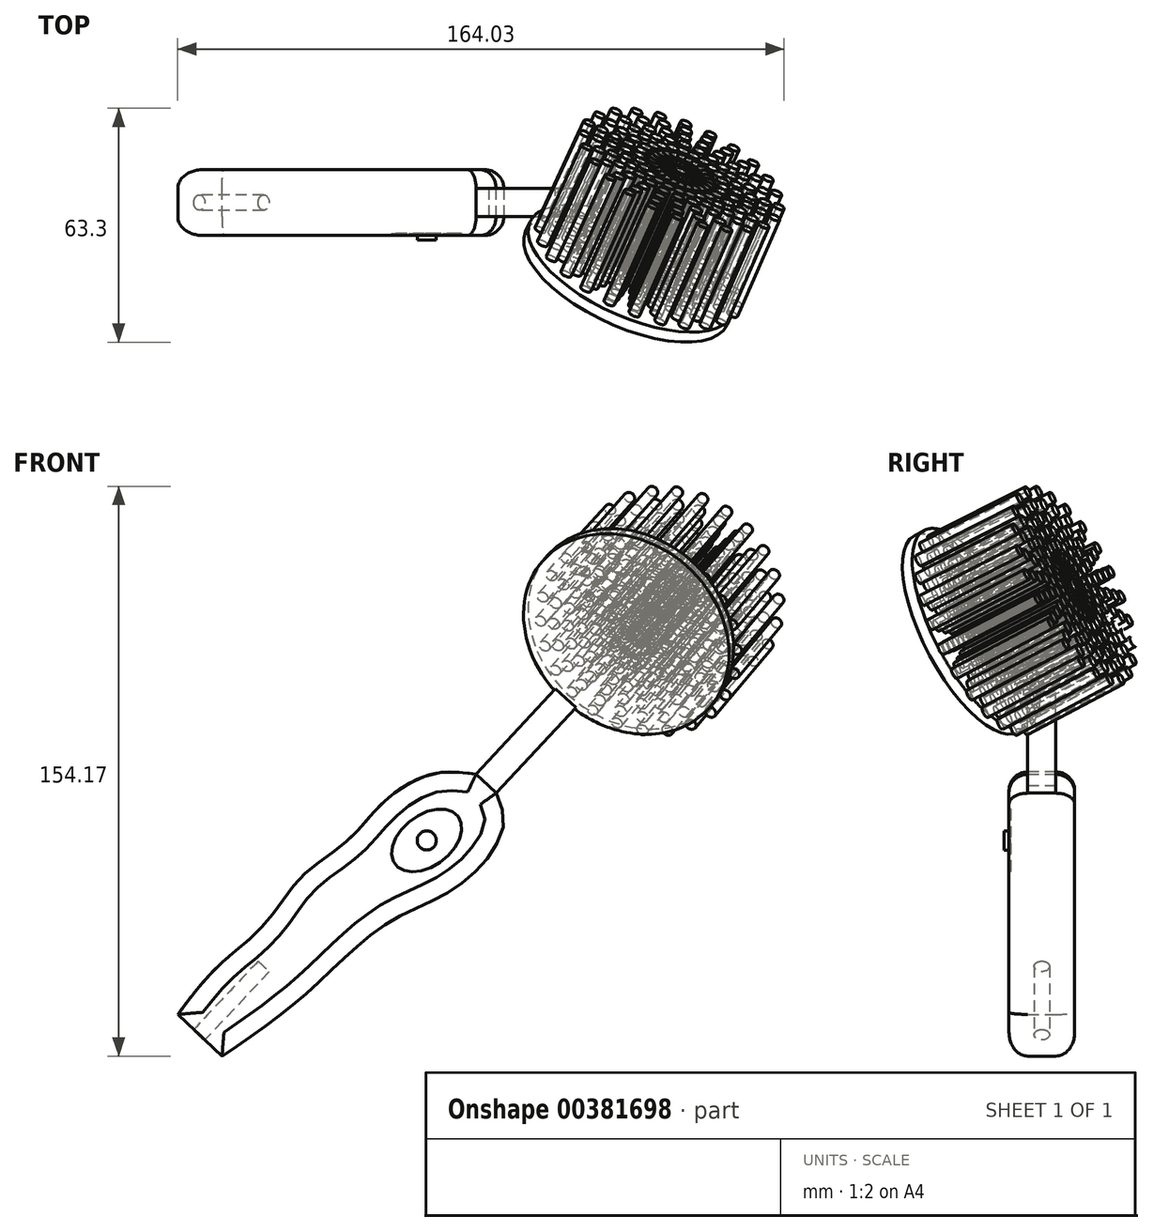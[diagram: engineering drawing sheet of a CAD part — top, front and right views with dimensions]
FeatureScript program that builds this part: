
annotation { "Feature Type Name" : "Feature", "Feature Type Description" : "" }
export const myFeature = defineFeature(function(context is Context, id is Id, definition is map)
    precondition{}
    {
        {
            var Q0;
            Q0=qCreatedBy(makeId("Front.planeOp"),FACE);
            var sketch = newSketch(context, id + "F0", { "sketchPlane" : qUnion([Q0])});
            skLineSegment(sketch, "E0", {"start": v(-5.4, 17.89) * mm, "end": v(0, 12.8) * mm});
            skLineSegment(sketch, "E1", {"start": v(-86.13, -47.06) * mm, "end": v(-74.15, -58.34) * mm});
            skFitSpline(sketch, "E2", {"points": [v(-86.13, -47.06) * mm, v(-75.3, -34.12) * mm, v(-62.36, -22.36) * mm, v(-53.18, -10.35) * mm, v(-40.24, 0) * mm, v(-29.65, 11.06) * mm, v(-16.7, 18.12) * mm, v(-5.4, 17.89) * mm], "startDerivative": vector(66.75, 89.58) * mm, "endDerivative": vector(90.32, -12.97) * mm});
            skFitSpline(sketch, "E3", {"points": [v(0, 12.8) * mm, v(1.88, 3.53) * mm, v(-10.12, -12.24) * mm, v(-29.42, -22.36) * mm, v(-51.3, -41.42) * mm, v(-74.15, -58.34) * mm], "startDerivative": vector(28.86, -64.08) * mm, "endDerivative": vector(-99.9, -67.33) * mm});
            skSolve(sketch);
        }
        {
            var Q0;
            Q0=makeQuery(id+"F0.imprint","IMPRINT",FACE,{"disambiguationData":[TD([[makeQuery(id+"F0.imprint","IMPRINT",EDGE,{"derivedFrom":sQuery(id+"F0.wireOp",EDGE,"E0")}),-1.0]])]});
            extrude(context, id + "F1", {"entities" : qUnion([Q0]), "depth" : 8.9 * mm});
        }
        {
            var Q0;
            Q0=makeQuery(id+"F1.opExtrude","CAP_FACE",FACE,{"disambiguationData":[OSD([sQuery(id+"F0.wireOp",EDGE,"E0"),sQuery(id+"F0.wireOp",EDGE,"E1"),sQuery(id+"F0.wireOp",EDGE,"E2"),sQuery(id+"F0.wireOp",EDGE,"E3")])],"isStart":true});
            extrude(context, id + "F2", {"entities" : qUnion([Q0]), "operationType" : NewBodyOperationType.ADD, "depth" : 8.9 * mm});
        }
        {
            var Q0;
            Q0=makeQuery(id+"F1.opExtrude","CAP_FACE",FACE,{"disambiguationData":[OSD([sQuery(id+"F0.wireOp",EDGE,"E0"),sQuery(id+"F0.wireOp",EDGE,"E1"),sQuery(id+"F0.wireOp",EDGE,"E2"),sQuery(id+"F0.wireOp",EDGE,"E3")])],"isStart":false});
            var Q1;
            Q1=makeQuery(id+"F2.opExtrude","CAP_FACE",FACE,{"disambiguationData":[OSD([sQuery(id+"F0.wireOp",EDGE,"E0"),sQuery(id+"F0.wireOp",EDGE,"E1"),sQuery(id+"F0.wireOp",EDGE,"E2"),sQuery(id+"F0.wireOp",EDGE,"E3")])],"isStart":false});
            fillet(context, id + "F3", {"entities" : qUnion([Q0, Q1]), "radius" : 5.08 * mm, "tangentPropagation" : true, "allowEdgeOverflow" : false});
        }
        {
            var Q0;
            Q0=qCreatedBy(makeId("Front.planeOp"),FACE);
            var sketch = newSketch(context, id + "F4", { "sketchPlane" : qUnion([Q0])});
            skLineSegment(sketch, "E4", {"start": v(-5.42, 17.88) * mm, "end": v(16, 41) * mm});
            skLineSegment(sketch, "E5", {"start": v(0, 12.81) * mm, "end": v(21.66, 36.03) * mm});
            skLineSegment(sketch, "E6", {"start": v(21.66, 36.03) * mm, "end": v(16, 41) * mm});
            skLineSegment(sketch, "E7", {"start": v(-5.42, 17.88) * mm, "end": v(0, 12.81) * mm});
            skSolve(sketch);
        }
        {
            var Q0;
            Q0=makeQuery(id+"F4.imprint","IMPRINT",FACE,{"disambiguationData":[TD([[makeQuery(id+"F4.imprint","IMPRINT",EDGE,{"derivedFrom":sQuery(id+"F4.wireOp",EDGE,"E4")}),-1.0]])]});
            extrude(context, id + "F5", {"entities" : qUnion([Q0]), "operationType" : NewBodyOperationType.ADD, "depth" : 3.8 * mm});
        }
        {
            var Q0;
            Q0=makeQuery(id+"F5.opExtrude","CAP_FACE",FACE,{"disambiguationData":[OSD([sQuery(id+"F4.wireOp",EDGE,"E4"),sQuery(id+"F4.wireOp",EDGE,"E5"),sQuery(id+"F4.wireOp",EDGE,"E6"),sQuery(id+"F4.wireOp",EDGE,"E7")])],"isStart":true});
            extrude(context, id + "F6", {"entities" : qUnion([Q0]), "operationType" : NewBodyOperationType.ADD, "depth" : 3.8 * mm});
        }
        {
            var Q0;
            {var subQ0=sQuery(id+"F4.wireOp",EDGE,"E6");Q0=makeQuery(id+"F6.boolean.opBoolean","MERGE",FACE,{"derivedFrom":[makeQuery(id+"F5.opExtrude","SWEPT_FACE",FACE,{"disambiguationData":[OSD([subQ0])]}),makeQuery(id+"F6.opExtrude","SWEPT_FACE",FACE,{"disambiguationData":[OSD([subQ0])]})]});}
            var sketch = newSketch(context, id + "F7", { "sketchPlane" : qUnion([Q0])});
            skLineSegment(sketch, "E8", {"start": v(-11.33, 3.81) * mm, "end": v(-11.33, -3.81) * mm, "construction": true});
            skSolve(sketch);
        }
        {
            var Q0;
            Q0=makeQuery(id+"F5.opExtrude","CAP_EDGE",EDGE,{"disambiguationData":[OSD([sQuery(id+"F4.wireOp",EDGE,"E6")])],"isStart":false});
            cPlane(context, id + "F8", {"entities" : qUnion([Q0]), "cplaneType" : CPlaneType.LINE_ANGLE, "offset" : 25.4 * mm, "angle" : 35 * degree, "oppositeDirection" : true, "width" : 152.4 * mm, "height" : 152.4 * mm});
        }
        {
            var Q0;
            Q0=qCreatedBy(id+"F8.planeOp",FACE);
            var sketch = newSketch(context, id + "F9", { "sketchPlane" : qUnion([Q0])});
            skCircle(sketch, "E9", {"center": v(29.65, 59.02) * mm, "radius": 30.06 * mm});
            skSolve(sketch);
        }
        {
            var Q0;
            Q0=makeQuery(id+"F9.imprint","IMPRINT",FACE,{"disambiguationData":[TD([[makeQuery(id+"F9.imprint","IMPRINT",EDGE,{"derivedFrom":sQuery(id+"F9.wireOp",EDGE,"E9")}),1.0]])]});
            extrude(context, id + "F10", {"entities" : qUnion([Q0]), "operationType" : NewBodyOperationType.ADD, "oppositeDirection" : true, "depth" : 3.3 * mm});
        }
        {
            var Q0;
            Q0=makeQuery(id+"F10.opExtrude","CAP_FACE",FACE,{"disambiguationData":[OSD([sQuery(id+"F9.wireOp",EDGE,"E9")])],"isStart":false});
            var sketch = newSketch(context, id + "F11", { "sketchPlane" : qUnion([Q0])});
            skLineSegment(sketch, "E10", {"start": v(-50.72, 80.45) * mm, "end": v(-10.25, 36.04) * mm, "construction": true});
            skLineSegment(sketch, "E11", {"start": v(-30.49, 58.25) * mm, "end": v(-7.43, 79.26) * mm, "construction": true});
            skLineSegment(sketch, "E12", {"start": v(-30.49, 58.25) * mm, "end": v(-51.87, 38.77) * mm, "construction": true});
            skSolve(sketch);
        }
        {
            var Q0;
            Q0=makeQuery(id+"F11.imprint","IMPRINT",FACE,{"disambiguationData":[TD([[makeQuery(id+"F11.imprint","IMPRINT",EDGE,{"derivedFrom":makeQuery(id+"F10.opExtrude","CAP_EDGE",EDGE,{"disambiguationData":[OSD([sQuery(id+"F9.wireOp",EDGE,"E9")])],"isStart":false})}),-1.0]])]});
            cPlane(context, id + "F12", {"entities" : qUnion([Q0]), "cplaneType" : CPlaneType.OFFSET, "offset" : 31.75 * mm, "width" : 152.4 * mm, "height" : 152.4 * mm});
        }
        {
            var Q0;
            Q0=qCreatedBy(id+"F12.planeOp",FACE);
            var sketch = newSketch(context, id + "F13", { "sketchPlane" : qUnion([Q0])});
            skCircle(sketch, "E13", {"center": v(-31.35, 57.04) * mm, "radius": 1.65 * mm});
            skCircle(sketch, "E14", {"center": v(-28.64, 54) * mm, "radius": 1.65 * mm});
            skCircle(sketch, "E15", {"center": v(-26, 50.91) * mm, "radius": 1.65 * mm});
            skCircle(sketch, "E16", {"center": v(-23.19, 47.99) * mm, "radius": 1.65 * mm});
            skCircle(sketch, "E17", {"center": v(-20.63, 44.83) * mm, "radius": 1.65 * mm});
            skCircle(sketch, "E18", {"center": v(-17.78, 41.94) * mm, "radius": 1.65 * mm});
            skCircle(sketch, "E19", {"center": v(-15.07, 38.9) * mm, "radius": 1.65 * mm});
            skCircle(sketch, "E20", {"center": v(-12.28, 36.13) * mm, "radius": 1.52 * mm});
            skSolve(sketch);
        }
        {
            var Q0;
            Q0=makeQuery(id+"F13.imprint","IMPRINT",FACE,{"disambiguationData":[TD([[makeQuery(id+"F13.imprint","IMPRINT",EDGE,{"derivedFrom":sQuery(id+"F13.wireOp",EDGE,"E13")}),1.0]])]});
            var Q1;
            Q1=makeQuery(id+"F13.imprint","IMPRINT",FACE,{"disambiguationData":[TD([[makeQuery(id+"F13.imprint","IMPRINT",EDGE,{"derivedFrom":sQuery(id+"F13.wireOp",EDGE,"E14")}),1.0]])]});
            var Q2;
            Q2=makeQuery(id+"F13.imprint","IMPRINT",FACE,{"disambiguationData":[TD([[makeQuery(id+"F13.imprint","IMPRINT",EDGE,{"derivedFrom":sQuery(id+"F13.wireOp",EDGE,"E15")}),1.0]])]});
            var Q3;
            Q3=makeQuery(id+"F13.imprint","IMPRINT",FACE,{"disambiguationData":[TD([[makeQuery(id+"F13.imprint","IMPRINT",EDGE,{"derivedFrom":sQuery(id+"F13.wireOp",EDGE,"E16")}),1.0]])]});
            var Q4;
            Q4=makeQuery(id+"F13.imprint","IMPRINT",FACE,{"disambiguationData":[TD([[makeQuery(id+"F13.imprint","IMPRINT",EDGE,{"derivedFrom":sQuery(id+"F13.wireOp",EDGE,"E17")}),1.0]])]});
            var Q5;
            Q5=makeQuery(id+"F13.imprint","IMPRINT",FACE,{"disambiguationData":[TD([[makeQuery(id+"F13.imprint","IMPRINT",EDGE,{"derivedFrom":sQuery(id+"F13.wireOp",EDGE,"E18")}),1.0]])]});
            var Q6;
            Q6=makeQuery(id+"F13.imprint","IMPRINT",FACE,{"disambiguationData":[TD([[makeQuery(id+"F13.imprint","IMPRINT",EDGE,{"derivedFrom":sQuery(id+"F13.wireOp",EDGE,"E19")}),1.0]])]});
            var Q7;
            Q7=makeQuery(id+"F13.imprint","IMPRINT",FACE,{"disambiguationData":[TD([[makeQuery(id+"F13.imprint","IMPRINT",EDGE,{"derivedFrom":sQuery(id+"F13.wireOp",EDGE,"E20")}),1.0]])]});
            extrude(context, id + "F14", {"entities" : qUnion([Q0, Q1, Q2, Q3, Q4, Q5, Q6, Q7]), "operationType" : NewBodyOperationType.ADD, "oppositeDirection" : true, "depth" : 31.62 * mm});
        }
        {
            var Q0;
            Q0=qCreatedBy(id+"F12.planeOp",FACE);
            var sketch = newSketch(context, id + "F15", { "sketchPlane" : qUnion([Q0])});
            skPoint(sketch, "E21", {"position": v(-31.35, 57.04) * mm});
            skSolve(sketch);
        }
        {
            var Q0;
            Q0=sQuery(id+"F11.wireOp",EDGE,"E12");
            var Q1;
            Q1=sQuery(id+"F15.wireOp",VERTEX,"E21");
            cPlane(context, id + "F16", {"entities" : qUnion([Q0, Q1]), "cplaneType" : CPlaneType.LINE_ANGLE, "offset" : 25.4 * mm, "angle" : 0 * degree, "width" : 152.4 * mm, "height" : 152.4 * mm});
        }
        {
            var Q0;
            Q0=qCreatedBy(id+"F16.planeOp",FACE);
            var sketch = newSketch(context, id + "F17", { "sketchPlane" : qUnion([Q0])});
            skLineSegment(sketch, "E22", {"start": v(-45.25, 93.19) * mm, "end": v(-30.63, 58.2) * mm, "construction": true});
            skLineSegment(sketch, "E23", {"start": v(53.65, 19.52) * mm, "end": v(22.06, 16.93) * mm, "construction": true});
            skSolve(sketch);
        }
        {
            var Q0;
            Q0=makeQuery(id+"F14.opExtrude","SWEPT_BODY",BODY,{"disambiguationData":[OSD([sQuery(id+"F13.wireOp",EDGE,"E13")])]});
            var Q1;
            Q1=makeQuery(id+"F14.opExtrude","SWEPT_BODY",BODY,{"disambiguationData":[OSD([sQuery(id+"F13.wireOp",EDGE,"E14")])]});
            var Q2;
            Q2=makeQuery(id+"F14.opExtrude","SWEPT_BODY",BODY,{"disambiguationData":[OSD([sQuery(id+"F13.wireOp",EDGE,"E15")])]});
            var Q3;
            Q3=makeQuery(id+"F14.opExtrude","SWEPT_BODY",BODY,{"disambiguationData":[OSD([sQuery(id+"F13.wireOp",EDGE,"E16")])]});
            var Q4;
            Q4=makeQuery(id+"F14.opExtrude","SWEPT_BODY",BODY,{"disambiguationData":[OSD([sQuery(id+"F13.wireOp",EDGE,"E17")])]});
            var Q5;
            Q5=makeQuery(id+"F14.opExtrude","SWEPT_BODY",BODY,{"disambiguationData":[OSD([sQuery(id+"F13.wireOp",EDGE,"E18")])]});
            var Q6;
            Q6=makeQuery(id+"F14.opExtrude","SWEPT_BODY",BODY,{"disambiguationData":[OSD([sQuery(id+"F13.wireOp",EDGE,"E19")])]});
            var Q7;
            Q7=makeQuery(id+"F14.opExtrude","SWEPT_BODY",BODY,{"disambiguationData":[OSD([sQuery(id+"F13.wireOp",EDGE,"E20")])]});
            var Q8;
            Q8=sQuery(id+"F17.wireOp",EDGE,"E23");
            circularPattern(context, id + "F18", {"entities" : qUnion([Q0, Q1, Q2, Q3, Q4, Q5, Q6, Q7]), "axis" : qUnion([Q8]), "angle" : 360 * degree, "instanceCount" : 24, "equalSpace" : true});
        }
        {
            var Q0;
            Q0=makeQuery(id+"F1.opExtrude","CAP_FACE",FACE,{"disambiguationData":[OSD([sQuery(id+"F0.wireOp",EDGE,"E0"),sQuery(id+"F0.wireOp",EDGE,"E1"),sQuery(id+"F0.wireOp",EDGE,"E2"),sQuery(id+"F0.wireOp",EDGE,"E3")])],"isStart":false});
            var sketch = newSketch(context, id + "F19", { "sketchPlane" : qUnion([Q0])});
            skCircle(sketch, "E24", {"center": v(-18.77, 0) * mm, "radius": 2.58 * mm});
            skEllipse(sketch, "E25", {"center": v(-18.77, 0) * mm, "majorRadius": 10.68 * mm, "minorRadius": 6.9 * mm, "majorAxis": v(0.8, 0.6)});
            skSolve(sketch);
        }
        {
            var Q0;
            Q0=makeQuery(id+"F19.imprint","IMPRINT",FACE,{"disambiguationData":[TD([[makeQuery(id+"F19.imprint","IMPRINT",EDGE,{"derivedFrom":sQuery(id+"F19.wireOp",EDGE,"E24")}),1.0]])]});
            extrude(context, id + "F20", {"entities" : qUnion([Q0]), "operationType" : NewBodyOperationType.ADD, "depth" : 1.27 * mm});
        }
        {
            var Q0;
            Q0 = qSketchRegion(id + "F19", true);
            extrude(context, id + "F21", {"entities" : qUnion([Q0]), "operationType" : NewBodyOperationType.REMOVE, "oppositeDirection" : true, "depth" : 0.5 * mm});
        }
        {
            var Q0;
            {var subQ0=sQuery(id+"F0.wireOp",EDGE,"E1");Q0=makeQuery(id+"F2.boolean.opBoolean","MERGE",FACE,{"derivedFrom":[makeQuery(id+"F1.opExtrude","SWEPT_FACE",FACE,{"disambiguationData":[OSD([subQ0])]}),makeQuery(id+"F2.opExtrude","SWEPT_FACE",FACE,{"disambiguationData":[OSD([subQ0])]})]});}
            var sketch = newSketch(context, id + "F22", { "sketchPlane" : qUnion([Q0])});
            skCircle(sketch, "E26", {"center": v(-22.44, 0) * mm, "radius": 2.07 * mm});
            skSolve(sketch);
        }
        {
            var Q0;
            Q0=makeQuery(id+"F22.imprint","IMPRINT",FACE,{"disambiguationData":[TD([[makeQuery(id+"F22.imprint","IMPRINT",EDGE,{"derivedFrom":sQuery(id+"F22.wireOp",EDGE,"E26")}),1.0]])]});
            extrude(context, id + "F23", {"entities" : qUnion([Q0]), "operationType" : NewBodyOperationType.REMOVE, "oppositeDirection" : true, "depth" : 25.4 * mm});
        }
    });
